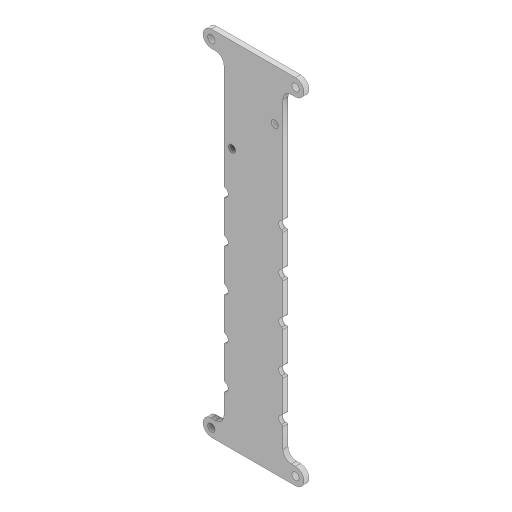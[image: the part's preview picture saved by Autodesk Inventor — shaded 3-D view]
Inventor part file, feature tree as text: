
AUTODESK INVENTOR PART (.ipt)
format: ipt  version: 2023 (Build 270158000, 158)  size: 212,480 bytes
history: native  units: mm
features: extrude x3, sketch x3, fillet x2, pattern_linear x1
ambient origin geometry x8: Origin, YZ Plane, XZ Plane, XY Plane, X Axis, Y Axis, Z Axis, Center Point
bodies: Solid1 (feature_tree)
feature tree (9):
  extrude  "Extrusion1"  Depth=35.0mm
  fillet  "Fillet1"  Radius=200.0mm
  extrude  "Extrusion2"  TaperAngle=0.0deg  [1 undecoded]
  extrude  "Extrusion3"  Depth=10.0mm
  fillet  "Fillet2"  Radius=10.0mm
  pattern_linear  "Rectangular Pattern1"  Spacing1=3.0mm  [1 undecoded]
  sketch  "Sketch1"  dims[d0=4.4mm d1=35.0mm d2=200.0mm]
  sketch  "Sketch2"  dims[d3=25.0mm d5=0.0mm]
  sketch  "Sketch3"  dims[d6=20.0mm d8=50.0mm d9=20.0mm d11=200.0mm d14=10.0mm d15=10.0mm d16=3.0mm d17=0.0mm d18=5.0mm d19=4.2mm d20=4.2mm d21=25.0mm d22=25.4mm d23=25.4mm d24=0.0mm d25=3.0mm d26=0.0mm d27=5.0mm d28=25.0mm d29=5.0mm d30=25.0mm d31=3.0mm d32=0.0mm d33=1.0mm d34=50.0mm d36=25.0mm]
note: 2 required parameter values undecoded (feature->parameter linkage not recoverable at this tier; creation-order binding heuristic only, values carry confidence <= 0.55)
